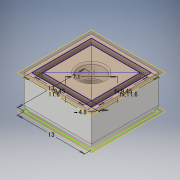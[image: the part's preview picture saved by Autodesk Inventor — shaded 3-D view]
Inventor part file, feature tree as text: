
AUTODESK INVENTOR PART (.ipt)
format: ipt  version: 2019.3 (Build 233278000, 278)  size: 164,352 bytes
history: native  units: in
note: dims shown in document units (in); Inventor stores cm internally (conversion verified against a paired STEP export)
features: extrude x4, fillet x3, sketch x2, other x1
ambient origin geometry x8: Origin, YZ Plane, XZ Plane, XY Plane, X Axis, Y Axis, Z Axis, Center Point
bodies: Body1 (feature_tree)
feature tree (10):
  other  "作業平面2"
  sketch  "スケッチ3"
  sketch  "スケッチ1"
  extrude  "押し出し8"  Depth=0.2559in
  extrude  "押し出し9"  Depth=0.372in
  extrude  "押し出し10"  Depth=0.372in
  extrude  "押し出し11"  Depth=0.4567in
  fillet  "フィレット2"  Radius=0.4567in
  fillet  "フィレット3"  Radius=0.2795in
  fillet  "フィレット4"  Radius=0.5118in
